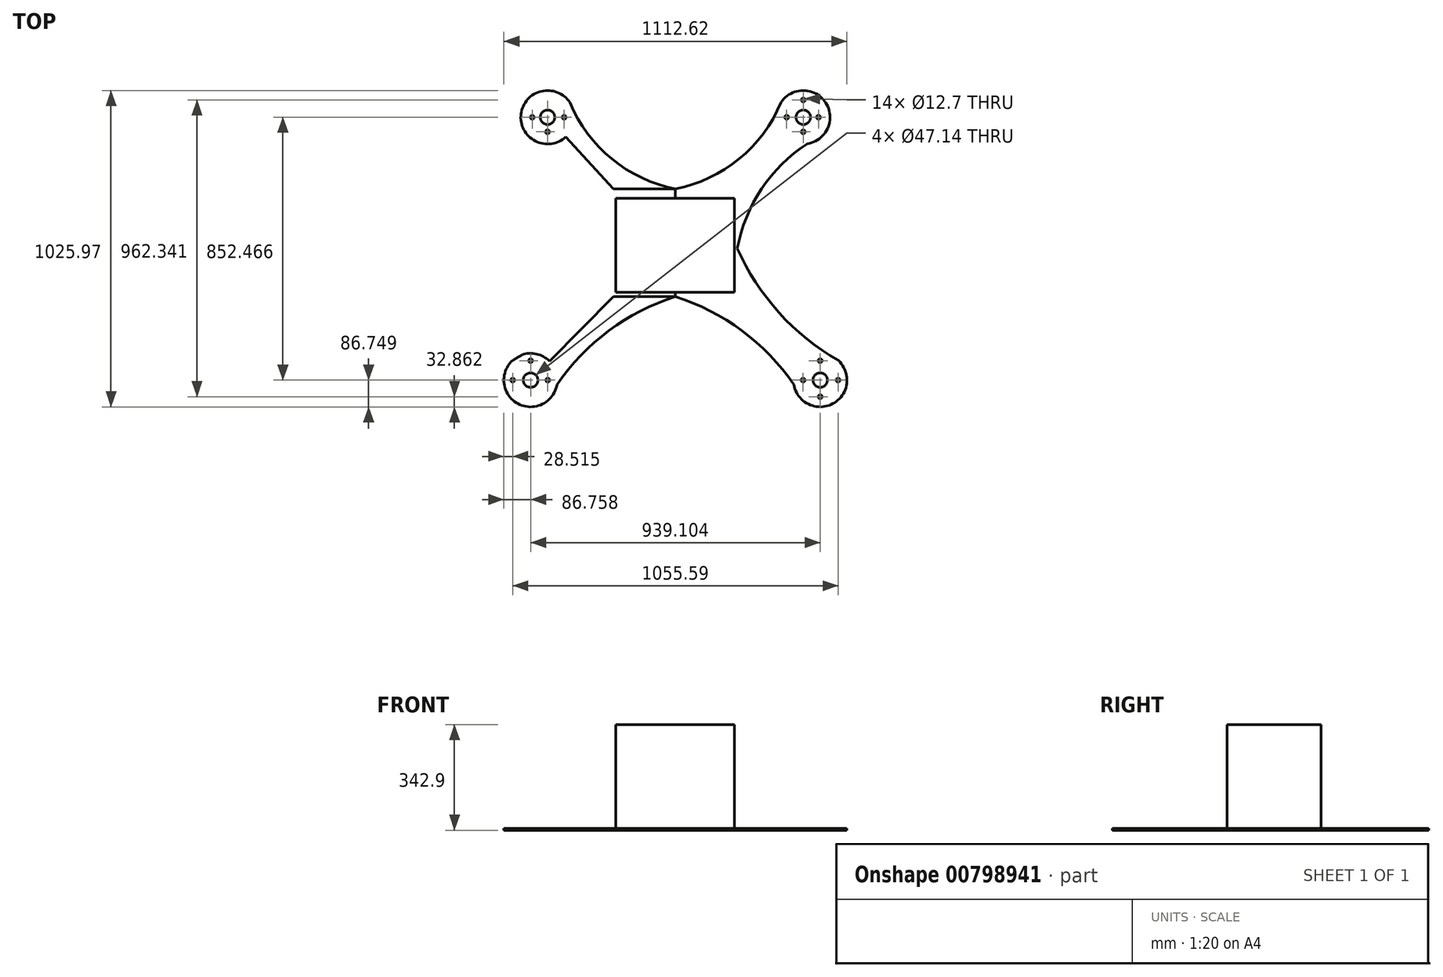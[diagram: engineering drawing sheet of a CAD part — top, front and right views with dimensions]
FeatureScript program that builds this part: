
annotation { "Feature Type Name" : "Feature", "Feature Type Description" : "" }
export const myFeature = defineFeature(function(context is Context, id is Id, definition is map)
    precondition{}
    {
        {
            var Q0;
            Q0=qCreatedBy(makeId("Top.planeOp"),FACE);
            var sketch = newSketch(context, id + "F0", { "sketchPlane" : qUnion([Q0])});
            skLineSegment(sketch, "E0.bottom", {"start": v(0, 99.42) * mm, "end": v(200.64, 99.42) * mm});
            skLineSegment(sketch, "E0.top", {"start": v(0, -249.98) * mm, "end": v(200.64, -249.98) * mm});
            skLineSegment(sketch, "E0.left", {"start": v(0, 99.42) * mm, "end": v(0, -249.98) * mm});
            skLineSegment(sketch, "E0.right", {"start": v(200.64, 99.42) * mm, "end": v(200.64, -249.98) * mm});
            skLineSegment(sketch, "E1", {"start": v(200.64, 99.42) * mm, "end": v(414.67, 331.74) * mm});
            skLineSegment(sketch, "E2", {"start": v(200.64, -249.98) * mm, "end": v(469.55, -520.72) * mm});
            skCircle(sketch, "E3", {"center": v(414.67, 331.74) * mm, "radius": 86.75 * mm});
            skCircle(sketch, "E4", {"center": v(469.55, -520.72) * mm, "radius": 86.75 * mm});
            skPoint(sketch, "E5.visualSharp", {"position": v(0, -249.98) * mm});
            skArc(sketch, "E6", {"start": v(0, 99.42) * mm, "mid": v(206.27, 196.58) * mm, "end": v(342.29, 379.56) * mm});
            skArc(sketch, "E7", {"start": v(481.37, 277.06) * mm, "mid": v(297.48, 124.63) * mm, "end": v(200.64, -93.7) * mm});
            skArc(sketch, "E8", {"start": v(200.64, -93.7) * mm, "mid": v(335.9, -301.65) * mm, "end": v(528.93, -457.47) * mm});
            skCircle(sketch, "E9", {"center": v(149.84, 35.58) * mm, "radius": 12.7 * mm});
            skCircle(sketch, "E10", {"center": v(149.84, -186.03) * mm, "radius": 12.7 * mm});
            skCircle(sketch, "E11", {"center": v(414.67, 331.74) * mm, "radius": 23.57 * mm});
            skCircle(sketch, "E12", {"center": v(469.55, -520.72) * mm, "radius": 23.57 * mm});
            skCircle(sketch, "E13", {"center": v(469.55, -457.73) * mm, "radius": 6.35 * mm});
            skCircle(sketch, "E14", {"center": v(469.55, -574.6) * mm, "radius": 6.35 * mm});
            skCircle(sketch, "E15", {"center": v(413.95, -520.72) * mm, "radius": 6.35 * mm});
            skCircle(sketch, "E16", {"center": v(527.8, -520.72) * mm, "radius": 6.35 * mm});
            skCircle(sketch, "E17", {"center": v(360.83, 331.74) * mm, "radius": 6.35 * mm});
            skCircle(sketch, "E18", {"center": v(414.67, 387.73) * mm, "radius": 6.35 * mm});
            skCircle(sketch, "E19", {"center": v(464.04, 331.74) * mm, "radius": 6.35 * mm});
            skCircle(sketch, "E20", {"center": v(414.67, 284.52) * mm, "radius": 6.35 * mm});
            skLineSegment(sketch, "E21.left", {"start": v(84.57, 20.4) * mm, "end": v(84.57, -172.37) * mm});
            skLineSegment(sketch, "E22", {"start": v(84.57, 20.4) * mm, "end": v(0, 20.4) * mm});
            skLineSegment(sketch, "E23", {"start": v(84.57, -172.37) * mm, "end": v(0, -172.37) * mm});
            skCircle(sketch, "E24.MirrorC", {"center": v(-414.67, 387.73) * mm, "radius": 6.35 * mm});
            skCircle(sketch, "E25.MirrorC", {"center": v(-469.55, -574.6) * mm, "radius": 6.35 * mm});
            skCircle(sketch, "E26.MirrorC", {"center": v(-469.55, -457.73) * mm, "radius": 6.35 * mm});
            skCircle(sketch, "E27.MirrorC", {"center": v(-360.83, 331.74) * mm, "radius": 6.35 * mm});
            skCircle(sketch, "E28.MirrorC", {"center": v(-464.04, 331.74) * mm, "radius": 6.35 * mm});
            skCircle(sketch, "E29.MirrorC", {"center": v(-413.95, -520.72) * mm, "radius": 6.35 * mm});
            skCircle(sketch, "E30.MirrorC", {"center": v(-414.67, 284.52) * mm, "radius": 6.35 * mm});
            skCircle(sketch, "E31.MirrorC", {"center": v(-527.8, -520.72) * mm, "radius": 6.35 * mm});
            skLineSegment(sketch, "E32.MirrorCS", {"start": v(-200.64, 99.42) * mm, "end": v(-200.64, -249.98) * mm});
            skCircle(sketch, "E33.MirrorC", {"center": v(-414.67, 331.74) * mm, "radius": 23.57 * mm});
            skLineSegment(sketch, "E34.MirrorCS", {"start": v(-200.64, -249.98) * mm, "end": v(-469.55, -520.72) * mm});
            skArc(sketch, "E35.MirrorCS", {"start": v(-481.37, 277.06) * mm, "mid": v(-297.48, 124.63) * mm, "end": v(-200.64, -93.7) * mm});
            skCircle(sketch, "E36.MirrorC", {"center": v(-149.84, 35.58) * mm, "radius": 12.7 * mm});
            skLineSegment(sketch, "E37.MirrorCS", {"start": v(-84.57, 20.4) * mm, "end": v(0, 20.4) * mm});
            skLineSegment(sketch, "E38.MirrorCS", {"start": v(-84.57, 20.4) * mm, "end": v(-84.57, -172.37) * mm});
            skLineSegment(sketch, "E39.MirrorCS", {"start": v(-200.64, 99.42) * mm, "end": v(-414.67, 331.74) * mm});
            skArc(sketch, "E40.MirrorCS", {"start": v(-200.64, -93.7) * mm, "mid": v(-335.9, -301.65) * mm, "end": v(-528.93, -457.47) * mm});
            skLineSegment(sketch, "E41.MirrorCS", {"start": v(0, -249.98) * mm, "end": v(-200.64, -249.98) * mm});
            skArc(sketch, "E42.MirrorCS", {"start": v(0, 99.42) * mm, "mid": v(-206.27, 196.58) * mm, "end": v(-342.29, 379.56) * mm});
            skLineSegment(sketch, "E43.MirrorCS", {"start": v(0, 99.42) * mm, "end": v(-200.64, 99.42) * mm});
            skCircle(sketch, "E44.MirrorC", {"center": v(-469.55, -520.72) * mm, "radius": 23.57 * mm});
            skCircle(sketch, "E45.MirrorC", {"center": v(-414.67, 331.74) * mm, "radius": 86.75 * mm});
            skLineSegment(sketch, "E46.MirrorCS", {"start": v(-84.57, -172.37) * mm, "end": v(0, -172.37) * mm});
            skCircle(sketch, "E47.MirrorC", {"center": v(-469.55, -520.72) * mm, "radius": 86.75 * mm});
            skCircle(sketch, "E48.MirrorC", {"center": v(-149.84, -186.03) * mm, "radius": 12.7 * mm});
            skArc(sketch, "E49", {"start": v(0, -249.98) * mm, "mid": v(-215.7, -360.6) * mm, "end": v(-384, -535.06) * mm});
            skArc(sketch, "E50.MirrorCS", {"start": v(0, -249.98) * mm, "mid": v(215.7, -360.6) * mm, "end": v(384, -535.06) * mm});
            skSolve(sketch);
        }
        {
            var Q0;
            Q0=makeQuery(id+"F0.imprint","IMPRINT",FACE,{"disambiguationData":[TD([[makeQuery(id+"F0.imprint","IMPRINT",EDGE,{"derivedFrom":sQuery(id+"F0.wireOp",EDGE,"E36.MirrorC")}),1.0]])]});
            var Q1;
            Q1=makeQuery(id+"F0.imprint","IMPRINT",FACE,{"disambiguationData":[TD([[makeQuery(id+"F0.imprint","IMPRINT",EDGE,{"derivedFrom":sQuery(id+"F0.wireOp",EDGE,"E12")}),-1.0]])]});
            var Q2;
            {var subQ0=sQuery(id+"F0.wireOp",EDGE,"E2");var subQ5=sQuery(id+"F0.wireOp",EDGE,"E4");var subQ6=makeQuery(id+"F0.imprint","INTERSECT",VERTEX,{"derivedFrom":[subQ0,subQ5]});Q2=makeQuery(id+"F0.imprint","IMPRINT",FACE,{"disambiguationData":[TD([[makeQuery(id+"F0.imprint","IMPRINT",EDGE,{"disambiguationData":[TD([[subQ6,1.0]])],"derivedFrom":subQ5}),-1.0]])]});}
            var Q3;
            {var subQ3=sQuery(id+"F0.wireOp",EDGE,"E0.bottom");Q3=makeQuery(id+"F0.imprint","IMPRINT",FACE,{"disambiguationData":[TD([[makeQuery(id+"F0.imprint","IMPRINT",EDGE,{"derivedFrom":subQ3}),-1.0]])]});}
            var Q4;
            {var subQ3=sQuery(id+"F0.wireOp",EDGE,"E7");var subQ5=sQuery(id+"F0.wireOp",EDGE,"E3");var subQ7=makeQuery(id+"F0.imprint","INTERSECT",VERTEX,{"derivedFrom":[subQ5,subQ3]});Q4=makeQuery(id+"F0.imprint","IMPRINT",FACE,{"disambiguationData":[TD([[makeQuery(id+"F0.imprint","IMPRINT",EDGE,{"disambiguationData":[TD([[subQ7,1.0]])],"derivedFrom":subQ5}),-1.0]])]});}
            var Q5;
            {var subQ0=sQuery(id+"F0.wireOp",EDGE,"E0.bottom");Q5=makeQuery(id+"F0.imprint","IMPRINT",FACE,{"disambiguationData":[TD([[makeQuery(id+"F0.imprint","IMPRINT",EDGE,{"derivedFrom":subQ0}),1.0]])]});}
            var Q6;
            {var subQ0=sQuery(id+"F0.wireOp",EDGE,"E43.MirrorCS");Q6=makeQuery(id+"F0.imprint","IMPRINT",FACE,{"disambiguationData":[TD([[makeQuery(id+"F0.imprint","IMPRINT",EDGE,{"derivedFrom":subQ0}),-1.0]])]});}
            var Q7;
            {var subQ3=sQuery(id+"F0.wireOp",EDGE,"E35.MirrorCS");var subQ5=sQuery(id+"F0.wireOp",EDGE,"E45.MirrorC");var subQ6=makeQuery(id+"F0.imprint","INTERSECT",VERTEX,{"derivedFrom":[subQ3,subQ5]});Q7=makeQuery(id+"F0.imprint","IMPRINT",FACE,{"disambiguationData":[TD([[makeQuery(id+"F0.imprint","IMPRINT",EDGE,{"disambiguationData":[TD([[subQ6,1.0]])],"derivedFrom":subQ5}),1.0]])]});}
            var Q8;
            {var subQ0=sQuery(id+"F0.wireOp",EDGE,"E34.MirrorCS");var subQ5=sQuery(id+"F0.wireOp",EDGE,"E47.MirrorC");var subQ6=makeQuery(id+"F0.imprint","INTERSECT",VERTEX,{"derivedFrom":[subQ0,subQ5]});Q8=makeQuery(id+"F0.imprint","IMPRINT",FACE,{"disambiguationData":[TD([[makeQuery(id+"F0.imprint","IMPRINT",EDGE,{"disambiguationData":[TD([[subQ6,1.0]])],"derivedFrom":subQ5}),1.0]])]});}
            var Q9;
            Q9=makeQuery(id+"F0.imprint","IMPRINT",FACE,{"disambiguationData":[TD([[makeQuery(id+"F0.imprint","IMPRINT",EDGE,{"derivedFrom":sQuery(id+"F0.wireOp",EDGE,"E25.MirrorC")}),1.0]])]});
            var Q10;
            Q10=makeQuery(id+"F0.imprint","IMPRINT",FACE,{"disambiguationData":[TD([[makeQuery(id+"F0.imprint","IMPRINT",EDGE,{"derivedFrom":sQuery(id+"F0.wireOp",EDGE,"E11")}),-1.0]])]});
            var Q11;
            Q11=makeQuery(id+"F0.imprint","IMPRINT",FACE,{"disambiguationData":[TD([[makeQuery(id+"F0.imprint","IMPRINT",EDGE,{"derivedFrom":sQuery(id+"F0.wireOp",EDGE,"E24.MirrorC")}),1.0]])]});
            var Q12;
            {var subQ0=sQuery(id+"F0.wireOp",EDGE,"E41.MirrorCS");Q12=makeQuery(id+"F0.imprint","IMPRINT",FACE,{"disambiguationData":[TD([[makeQuery(id+"F0.imprint","IMPRINT",EDGE,{"derivedFrom":subQ0}),1.0]])]});}
            var Q13;
            {var subQ0=sQuery(id+"F0.wireOp",EDGE,"E0.top");Q13=makeQuery(id+"F0.imprint","IMPRINT",FACE,{"disambiguationData":[TD([[makeQuery(id+"F0.imprint","IMPRINT",EDGE,{"derivedFrom":subQ0}),-1.0]])]});}
            extrude(context, id + "F1", {"entities" : qUnion([Q0, Q1, Q2, Q3, Q4, Q5, Q6, Q7, Q8, Q9, Q10, Q11, Q12, Q13]), "depth" : 6.35 * mm, "offsetDistance" : 25.4 * mm});
        }
        {
            var Q0;
            Q0=qCreatedBy(makeId("Top.planeOp"),FACE);
            var sketch = newSketch(context, id + "F2", { "sketchPlane" : qUnion([Q0])});
            skLineSegment(sketch, "E51.bottom", {"start": v(-193.37, 69.53) * mm, "end": v(190.82, 69.53) * mm});
            skLineSegment(sketch, "E51.top", {"start": v(-193.37, -235.53) * mm, "end": v(190.82, -235.53) * mm});
            skLineSegment(sketch, "E51.left", {"start": v(-193.37, 69.53) * mm, "end": v(-193.37, -235.53) * mm});
            skLineSegment(sketch, "E51.right", {"start": v(190.82, 69.53) * mm, "end": v(190.82, -235.53) * mm});
            skSolve(sketch);
        }
        {
            var Q0;
            Q0 = qSketchRegion(id + "F2", true);
            extrude(context, id + "F3", {"entities" : qUnion([Q0]), "operationType" : NewBodyOperationType.ADD, "surfaceOperationType" : NewSurfaceOperationType.ADD, "depth" : 342.9 * mm, "offsetDistance" : 25.4 * mm});
        }
    });
